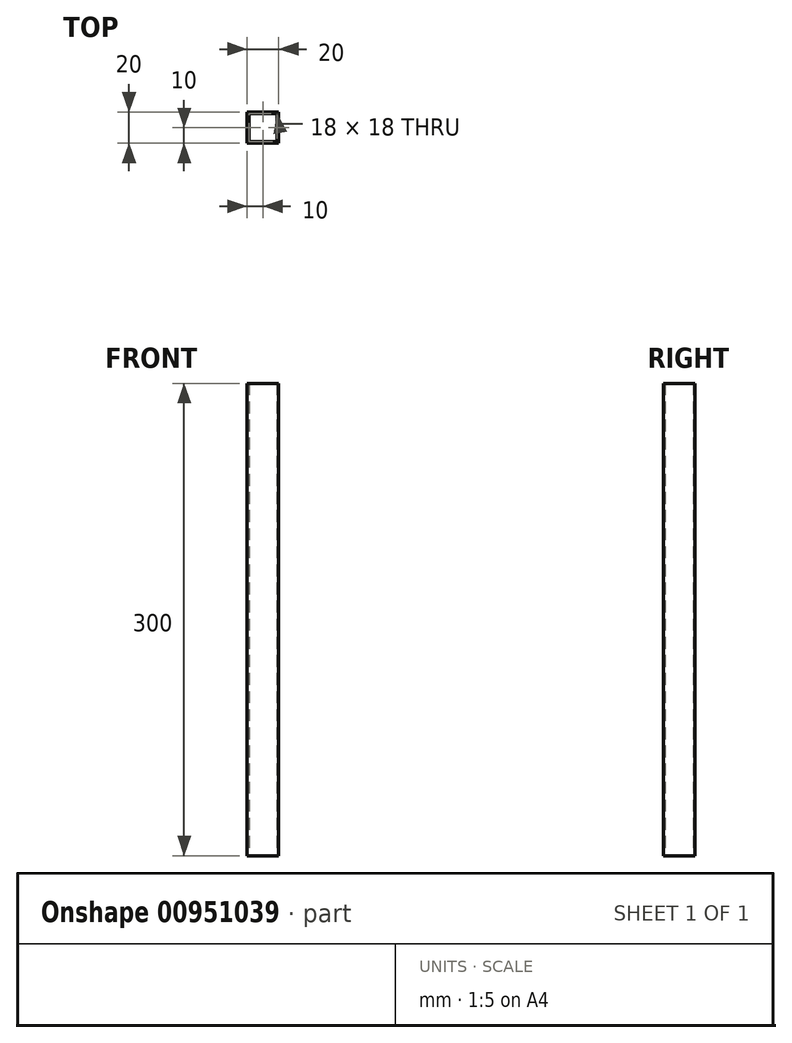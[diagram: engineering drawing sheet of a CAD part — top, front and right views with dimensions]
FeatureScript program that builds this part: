
annotation { "Feature Type Name" : "Feature", "Feature Type Description" : "" }
export const myFeature = defineFeature(function(context is Context, id is Id, definition is map)
    precondition{}
    {
        {
            var Q0;
            Q0=qCreatedBy(makeId("Top.planeOp"),FACE);
            var sketch = newSketch(context, id + "F0", { "sketchPlane" : qUnion([Q0])});
            skLineSegment(sketch, "E0.bottom", {"start": v(10, 10) * mm, "end": v(-10, 10) * mm});
            skLineSegment(sketch, "E0.top", {"start": v(10, -10) * mm, "end": v(-10, -10) * mm});
            skLineSegment(sketch, "E0.left", {"start": v(10, 10) * mm, "end": v(10, -10) * mm});
            skLineSegment(sketch, "E0.right", {"start": v(-10, 10) * mm, "end": v(-10, -10) * mm});
            skPoint(sketch, "E0.middle", {"position": v(0, 0) * mm});
            skLineSegment(sketch, "E1.bottom", {"start": v(9, 9) * mm, "end": v(-9, 9) * mm});
            skLineSegment(sketch, "E1.top", {"start": v(9, -9) * mm, "end": v(-9, -9) * mm});
            skLineSegment(sketch, "E1.left", {"start": v(9, 9) * mm, "end": v(9, -9) * mm});
            skLineSegment(sketch, "E1.right", {"start": v(-9, 9) * mm, "end": v(-9, -9) * mm});
            skSolve(sketch);
        }
        {
            var Q0;
            Q0=makeQuery(id+"F0.imprint","IMPRINT",FACE,{"disambiguationData":[TD([[makeQuery(id+"F0.imprint","IMPRINT",EDGE,{"derivedFrom":sQuery(id+"F0.wireOp",EDGE,"E0.bottom")}),1.0]])]});
            extrude(context, id + "F1", {"entities" : qUnion([Q0]), "depth" : 300 * mm, "offsetDistance" : 25 * mm});
        }
    });
